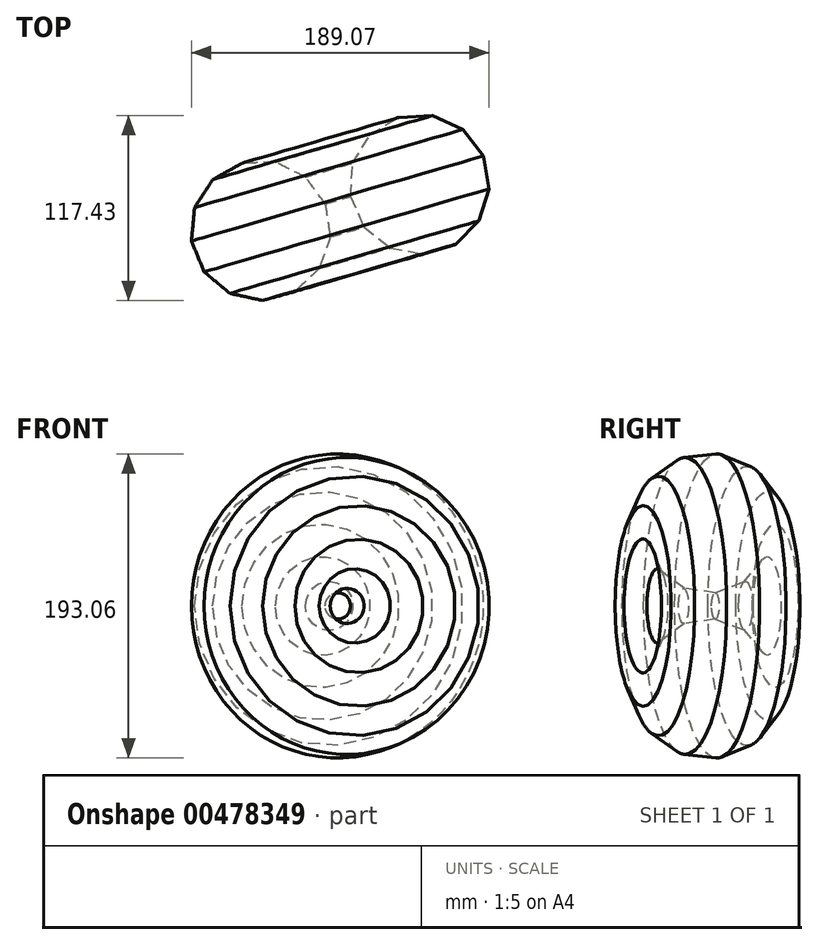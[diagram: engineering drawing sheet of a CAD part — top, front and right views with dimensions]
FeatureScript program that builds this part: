
annotation { "Feature Type Name" : "Feature", "Feature Type Description" : "" }
export const myFeature = defineFeature(function(context is Context, id is Id, definition is map)
    precondition{}
    {
        {
            var Q0;
            Q0=qCreatedBy(makeId("Top.planeOp"),FACE);
            var sketch = newSketch(context, id + "F0", { "sketchPlane" : qUnion([Q0])});
            skLineSegment(sketch, "E0", {"start": v(-52.2, 24.9) * mm, "end": v(10.95, 46.3) * mm});
            skFitSpline(sketch, "E1", {"points": [v(-52.2, 24.9) * mm, v(-55.8, 18.4) * mm, v(-46.55, 3.68) * mm, v(-45.52, 12.58) * mm, v(-36.97, 15.49) * mm, v(-34.57, 12.07) * mm, v(-34.4, 4.54) * mm, v(-36.11, -1.45) * mm, v(-34.4, -11.04) * mm, v(-30.8, -15.15) * mm, v(-27.55, -15.83) * mm, v(-23.45, -12.4) * mm, v(-21.4, -5.22) * mm, v(-22.25, 0) * mm, v(-23.62, 2.65) * mm, v(-26.87, 5.22) * mm, v(-30.3, 8.13) * mm, v(-28.4, 10.18) * mm, v(-26.19, 11.2) * mm, v(-13.7, 13.95) * mm, v(-13, 13.95) * mm, v(-8.04, 7.27) * mm, v(-8.04, 5.73) * mm, v(-10.78, 1.8) * mm, v(-11.8, -4.36) * mm, v(-11.12, -8.3) * mm, v(-7.53, -9.33) * mm, v(-2.4, -11.72) * mm, v(1.37, -12.24) * mm, v(4.28, -11.04) * mm, v(9.24, -9.16) * mm, v(9.58, -4.54) * mm, v(10.27, 1.63) * mm, v(11.98, 8.13) * mm, v(13.52, 12.24) * mm, v(13.7, 16.69) * mm, v(13.18, 20.28) * mm, v(7.53, 34.49) * mm, v(14.72, 42.02) * mm, v(10.95, 46.3) * mm], "startDerivative": vector(-209.56, -154.75) * mm, "endDerivative": vector(-247.68, 164.3) * mm});
            skSolve(sketch);
        }
        {
            var Q0;
            Q0=qCreatedBy(makeId("Front.planeOp"),FACE);
            var sketch = newSketch(context, id + "F1", { "sketchPlane" : qUnion([Q0])});
            skCircle(sketch, "E2.cCircle", {"center": v(0, 0) * mm, "radius": 23.38 * mm, "construction": true});
            skLineSegment(sketch, "E2.0", {"start": v(23.49, -40.44) * mm, "end": v(-46.76, -0.12) * mm});
            skLineSegment(sketch, "E2.1", {"start": v(-46.76, -0.12) * mm, "end": v(23.28, 40.56) * mm});
            skLineSegment(sketch, "E2.2", {"start": v(23.28, 40.56) * mm, "end": v(23.49, -40.44) * mm});
            skPoint(sketch, "E2.0.midPoint", {"position": v(-11.64, -20.28) * mm});
            skSolve(sketch);
        }
        {
            var Q0;
            Q0=qCreatedBy(makeId("Top.planeOp"),FACE);
            var sketch = newSketch(context, id + "F2", { "sketchPlane" : qUnion([Q0])});
            skCircle(sketch, "E3.cCircle", {"center": v(13.52, -12.92) * mm, "radius": 44.4 * mm, "construction": true});
            skLineSegment(sketch, "E3.0", {"start": v(21.74, 30.72) * mm, "end": v(41.08, 21.9) * mm});
            skLineSegment(sketch, "E3.1", {"start": v(41.08, 21.9) * mm, "end": v(54.1, 5.1) * mm});
            skLineSegment(sketch, "E3.2", {"start": v(54.1, 5.1) * mm, "end": v(57.83, -15.82) * mm});
            skLineSegment(sketch, "E3.3", {"start": v(57.83, -15.82) * mm, "end": v(51.41, -36.08) * mm});
            skLineSegment(sketch, "E3.4", {"start": v(51.41, -36.08) * mm, "end": v(36.31, -51.04) * mm});
            skLineSegment(sketch, "E3.5", {"start": v(36.31, -51.04) * mm, "end": v(15.99, -57.26) * mm});
            skLineSegment(sketch, "E3.6", {"start": v(15.99, -57.26) * mm, "end": v(-4.9, -53.33) * mm});
            skLineSegment(sketch, "E3.7", {"start": v(-4.9, -53.33) * mm, "end": v(-21.57, -40.14) * mm});
            skLineSegment(sketch, "E3.8", {"start": v(-21.57, -40.14) * mm, "end": v(-30.2, -20.72) * mm});
            skLineSegment(sketch, "E3.9", {"start": v(-30.2, -20.72) * mm, "end": v(-28.81, 0.5) * mm});
            skLineSegment(sketch, "E3.10", {"start": v(-28.81, 0.5) * mm, "end": v(-17.73, 18.63) * mm});
            skLineSegment(sketch, "E3.11", {"start": v(-17.73, 18.63) * mm, "end": v(0.51, 29.54) * mm});
            skLineSegment(sketch, "E3.12", {"start": v(0.51, 29.54) * mm, "end": v(21.74, 30.72) * mm});
            skLineSegment(sketch, "E4", {"start": v(-56.65, 40.13) * mm, "end": v(-22.08, -78.47) * mm, "construction": true});
            skSolve(sketch);
        }
        {
            var Q0;
            Q0=makeQuery(id+"F2.imprint","IMPRINT",FACE,{"disambiguationData":[TD([[makeQuery(id+"F2.imprint","IMPRINT",EDGE,{"derivedFrom":sQuery(id+"F2.wireOp",EDGE,"E3.0")}),-1.0]])]});
            var Q1;
            Q1=sQuery(id+"F2.wireOp",EDGE,"E4");
            revolve(context, id + "F3", {"entities" : qUnion([Q0]), "axis" : qUnion([Q1]), "revolveType" : RevolveType.FULL});
        }
    });
